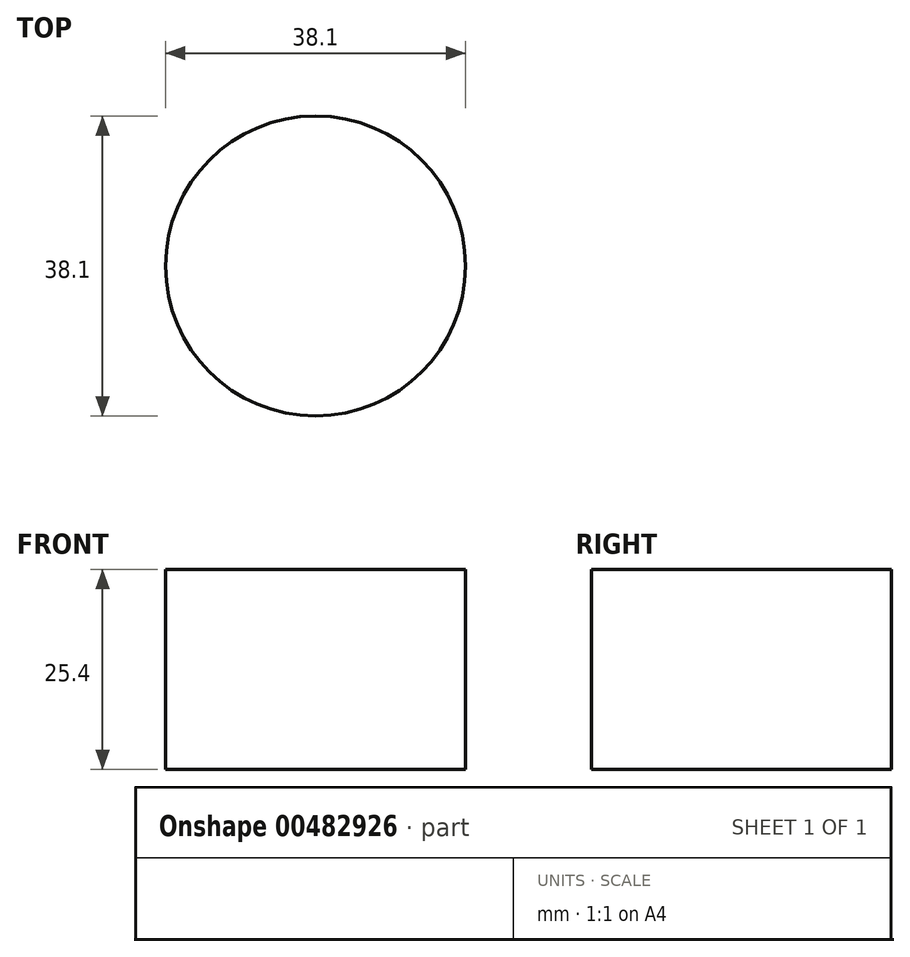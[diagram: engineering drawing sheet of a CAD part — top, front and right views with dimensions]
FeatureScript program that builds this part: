
annotation { "Feature Type Name" : "Feature", "Feature Type Description" : "" }
export const myFeature = defineFeature(function(context is Context, id is Id, definition is map)
    precondition{}
    {
        {
            var Q0;
            Q0=qCreatedBy(makeId("Top.planeOp"),FACE);
            var sketch = newSketch(context, id + "F0", { "sketchPlane" : qUnion([Q0])});
            skCircle(sketch, "E0", {"center": v(0, 0) * mm, "radius": 19.05 * mm});
            skSolve(sketch);
        }
        {
            var Q0;
            Q0 = qSketchRegion(id + "F0", true);
            var Q1;
            Q1=sQuery(id+"F0.wireOp",EDGE,"E0");
            extrude(context, id + "F1", {"entities" : qUnion([Q0]), "bodyType" : ToolBodyType.SURFACE, "surfaceEntities" : qUnion([Q1]), "depth" : 25.4 * mm, "offsetDistance" : 25.4 * mm});
        }
    });
